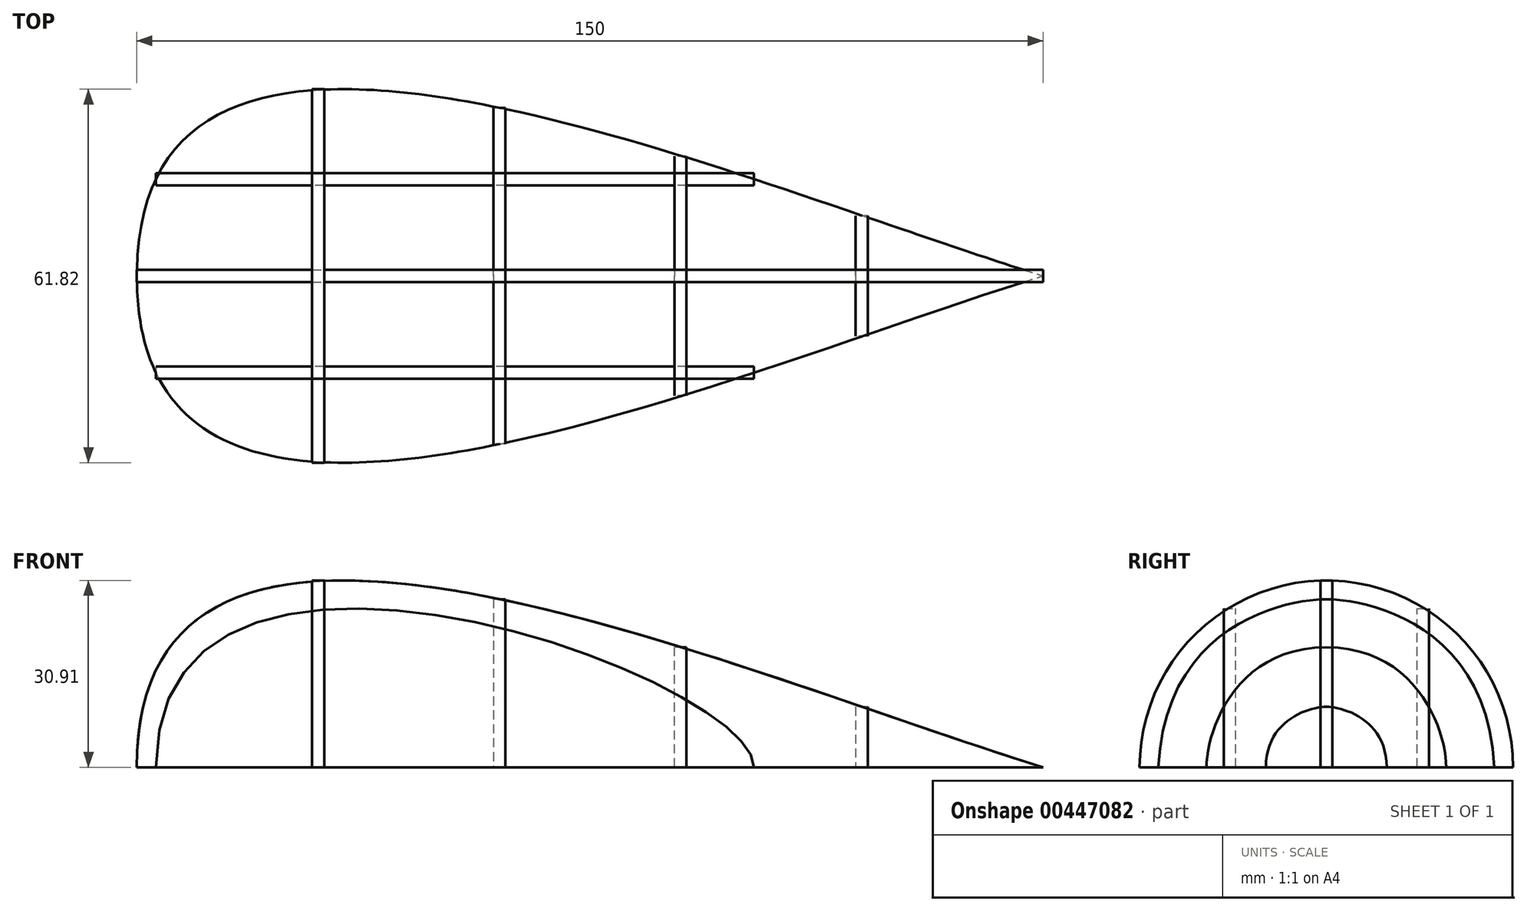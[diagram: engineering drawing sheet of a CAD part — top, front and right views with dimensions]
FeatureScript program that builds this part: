
annotation { "Feature Type Name" : "Feature", "Feature Type Description" : "" }
export const myFeature = defineFeature(function(context is Context, id is Id, definition is map)
    precondition{}
    {
        {
            var Q0;
            Q0=qCreatedBy(makeId("Front.planeOp"),FACE);
            var sketch = newSketch(context, id + "F0", { "sketchPlane" : qUnion([Q0])});
            skLineSegment(sketch, "E0", {"start": v(0, 0) * mm, "end": v(-75, 0) * mm});
            skLineSegment(sketch, "E1", {"start": v(0, 0) * mm, "end": v(0, -8.28) * mm, "construction": true});
            skLineSegment(sketch, "E2.MirrorCS", {"start": v(0, 0) * mm, "end": v(75, 0) * mm});
            skFitSpline(sketch, "E3", {"points": [v(-75, 0) * mm, v(75, 0) * mm], "startDerivative": vector(0, 179.74) * mm, "endDerivative": vector(167.07, -51.98) * mm});
            skSolve(sketch);
        }
        {
            var Q0;
            Q0=makeQuery(id+"F0.imprint","IMPRINT",FACE,{"disambiguationData":[TD([[makeQuery(id+"F0.imprint","IMPRINT",EDGE,{"derivedFrom":sQuery(id+"F0.wireOp",EDGE,"E0")}),-1.0]])]});
            var Q1;
            Q1=sQuery(id+"F0.wireOp",EDGE,"E0");
            revolve(context, id + "F1", {"surfaceOperationType" : NewSurfaceOperationType.NEW, "entities" : qUnion([Q0]), "axis" : qUnion([Q1]), "revolveType" : RevolveType.SYMMETRIC, "angle" : 180 * degree});
        }
        {
            var Q0;
            Q0=qCreatedBy(makeId("Right.planeOp"),FACE);
            cPlane(context, id + "F2", {"entities" : qUnion([Q0]), "cplaneType" : CPlaneType.OFFSET, "offset" : 75 * mm, "oppositeDirection" : true, "width" : 150 * mm, "height" : 150 * mm});
        }
        {
            var Q0;
            Q0=qCreatedBy(id+"F2.planeOp",FACE);
            cPlane(context, id + "F3", {"entities" : qUnion([Q0]), "cplaneType" : CPlaneType.OFFSET, "offset" : 30 * mm, "width" : 150 * mm, "height" : 150 * mm});
        }
        {
            var Q0;
            Q0=qCreatedBy(id+"F3.planeOp",FACE);
            cPlane(context, id + "F4", {"entities" : qUnion([Q0]), "cplaneType" : CPlaneType.OFFSET, "offset" : 30 * mm, "width" : 150 * mm, "height" : 150 * mm});
        }
        {
            var Q0;
            Q0=qCreatedBy(id+"F4.planeOp",FACE);
            cPlane(context, id + "F5", {"entities" : qUnion([Q0]), "cplaneType" : CPlaneType.OFFSET, "offset" : 30 * mm, "width" : 150 * mm, "height" : 150 * mm});
        }
        {
            var Q0;
            Q0=qCreatedBy(id+"F5.planeOp",FACE);
            cPlane(context, id + "F6", {"entities" : qUnion([Q0]), "cplaneType" : CPlaneType.OFFSET, "offset" : 30 * mm, "width" : 150 * mm, "height" : 150 * mm});
        }
        {
            var Q0;
            Q0=qCreatedBy(id+"F3.planeOp",FACE);
            var sketch = newSketch(context, id + "F7", { "sketchPlane" : qUnion([Q0])});
            skFitSpline(sketch, "E4.0", {"points": [v(0, 0) * mm, v(10.3, 0) * mm, v(20.6, 0) * mm, v(30.91, 0) * mm]});
            skFitSpline(sketch, "E5.0", {"points": [v(0, 0) * mm, v(-10.3, 0) * mm, v(-20.6, 0) * mm, v(-30.91, 0) * mm]});
            skArc(sketch, "E6", {"start": v(30.91, 0) * mm, "mid": v(0, 30.91) * mm, "end": v(-30.91, 0) * mm});
            skSolve(sketch);
        }
        {
            var Q0;
            Q0=qCreatedBy(id+"F4.planeOp",FACE);
            var sketch = newSketch(context, id + "F8", { "sketchPlane" : qUnion([Q0])});
            skLineSegment(sketch, "E7", {"start": v(0, 0) * mm, "end": v(27.82, 0) * mm});
            skLineSegment(sketch, "E8", {"start": v(0, 0) * mm, "end": v(0, 27.82) * mm, "construction": true});
            skFitSpline(sketch, "E9", {"points": [v(0, 27.82) * mm, v(27.82, 0) * mm], "startDerivative": vector(15.14, 0) * mm, "endDerivative": vector(3.77, -74.44) * mm});
            skFitSpline(sketch, "E10.MirrorCS", {"points": [v(0, 27.82) * mm, v(-27.82, 0) * mm], "startDerivative": vector(-15.14, 0) * mm, "endDerivative": vector(-3.77, -74.44) * mm});
            skLineSegment(sketch, "E11.MirrorCS", {"start": v(0, 0) * mm, "end": v(-27.82, 0) * mm});
            skSolve(sketch);
        }
        {
            var Q0;
            Q0=qCreatedBy(id+"F5.planeOp",FACE);
            var sketch = newSketch(context, id + "F9", { "sketchPlane" : qUnion([Q0])});
            skLineSegment(sketch, "E12", {"start": v(0, 0) * mm, "end": v(19.84, 0) * mm});
            skLineSegment(sketch, "E13", {"start": v(0, 0) * mm, "end": v(0, 19.84) * mm, "construction": true});
            skFitSpline(sketch, "E14", {"points": [v(19.84, 0) * mm, v(0, 19.84) * mm], "startDerivative": vector(0, 17.9) * mm, "endDerivative": vector(-45.4, 0) * mm});
            skFitSpline(sketch, "E15.MirrorCS", {"points": [v(-19.84, 0) * mm, v(0, 19.84) * mm], "startDerivative": vector(0, 17.9) * mm, "endDerivative": vector(45.4, 0) * mm});
            skLineSegment(sketch, "E16.MirrorCS", {"start": v(0, 0) * mm, "end": v(-19.84, 0) * mm});
            skSolve(sketch);
        }
        {
            var Q0;
            Q0=qCreatedBy(id+"F6.planeOp",FACE);
            var sketch = newSketch(context, id + "F10", { "sketchPlane" : qUnion([Q0])});
            skLineSegment(sketch, "E17", {"start": v(0, 0) * mm, "end": v(10, 0) * mm});
            skLineSegment(sketch, "E18", {"start": v(0, 0) * mm, "end": v(0, 10) * mm, "construction": true});
            skFitSpline(sketch, "E19", {"points": [v(0, 10) * mm, v(10, 0) * mm], "startDerivative": vector(9.17, 0) * mm, "endDerivative": vector(0, -23) * mm});
            skFitSpline(sketch, "E20.MirrorCS", {"points": [v(0, 10) * mm, v(-10, 0) * mm], "startDerivative": vector(-9.17, 0) * mm, "endDerivative": vector(0, -23) * mm});
            skLineSegment(sketch, "E21.MirrorCS", {"start": v(0, 0) * mm, "end": v(-10, 0) * mm});
            skSolve(sketch);
        }
        {
            var Q0;
            Q0=makeQuery(id+"F7.imprint","IMPRINT",FACE,{"disambiguationData":[TD([[makeQuery(id+"F7.imprint","IMPRINT",EDGE,{"derivedFrom":sQuery(id+"F7.wireOp",EDGE,"E4.0")}),1.0]])]});
            extrude(context, id + "F11", {"entities" : qUnion([Q0]), "endBound" : BoundingType.SYMMETRIC, "depth" : 2 * mm, "offsetDistance" : 25 * mm});
        }
        {
            var Q0;
            Q0=makeQuery(id+"F8.imprint","IMPRINT",FACE,{"disambiguationData":[TD([[makeQuery(id+"F8.imprint","IMPRINT",EDGE,{"derivedFrom":sQuery(id+"F8.wireOp",EDGE,"E7")}),1.0]])]});
            var Q1;
            Q1=makeQuery(id+"F9.imprint","IMPRINT",FACE,{"disambiguationData":[TD([[makeQuery(id+"F9.imprint","IMPRINT",EDGE,{"derivedFrom":sQuery(id+"F9.wireOp",EDGE,"E12")}),1.0]])]});
            var Q2;
            Q2=makeQuery(id+"F10.imprint","IMPRINT",FACE,{"disambiguationData":[TD([[makeQuery(id+"F10.imprint","IMPRINT",EDGE,{"derivedFrom":sQuery(id+"F10.wireOp",EDGE,"E17")}),1.0]])]});
            extrude(context, id + "F12", {"entities" : qUnion([Q0, Q1, Q2]), "endBound" : BoundingType.SYMMETRIC, "depth" : 2 * mm, "offsetDistance" : 25 * mm});
        }
        {
            var Q0;
            Q0=makeQuery(id+"F0.imprint","IMPRINT",FACE,{"disambiguationData":[TD([[makeQuery(id+"F0.imprint","IMPRINT",EDGE,{"derivedFrom":sQuery(id+"F0.wireOp",EDGE,"E0")}),-1.0]])]});
            extrude(context, id + "F13", {"entities" : qUnion([Q0]), "endBound" : BoundingType.SYMMETRIC, "depth" : 2 * mm, "offsetDistance" : 25 * mm});
        }
        {
            var Q0;
            Q0=qCreatedBy(makeId("Front.planeOp"),FACE);
            cPlane(context, id + "F14", {"entities" : qUnion([Q0]), "cplaneType" : CPlaneType.OFFSET, "offset" : 16 * mm, "oppositeDirection" : true, "width" : 150 * mm, "height" : 150 * mm});
        }
        {
            var Q0;
            Q0=qCreatedBy(id+"F14.planeOp",FACE);
            var sketch = newSketch(context, id + "F15", { "sketchPlane" : qUnion([Q0])});
            skLineSegment(sketch, "E22", {"start": v(27.18, 0) * mm, "end": v(-71.84, 0) * mm});
            skFitSpline(sketch, "E23", {"points": [v(27.18, 0) * mm, v(-71.84, 0) * mm], "startDerivative": vector(0, 45.02) * mm, "endDerivative": vector(0, -152.22) * mm});
            skSolve(sketch);
        }
        {
            var Q0;
            Q0 = qSketchRegion(id + "F15", true);
            extrude(context, id + "F16", {"entities" : qUnion([Q0]), "endBound" : BoundingType.SYMMETRIC, "depth" : 2 * mm, "offsetDistance" : 25 * mm});
        }
        {
            var Q0;
            Q0=makeQuery(id+"F16.opExtrude","SWEPT_BODY",BODY,{"disambiguationData":[OSD([sQuery(id+"F15.wireOp",EDGE,"E22"),sQuery(id+"F15.wireOp",EDGE,"E23")])]});
            var Q1;
            Q1=qCreatedBy(makeId("Front.planeOp"),FACE);
            mirror(context, id + "F17", {"entities" : qUnion([Q0]), "mirrorPlane" : qUnion([Q1])});
        }
    });
